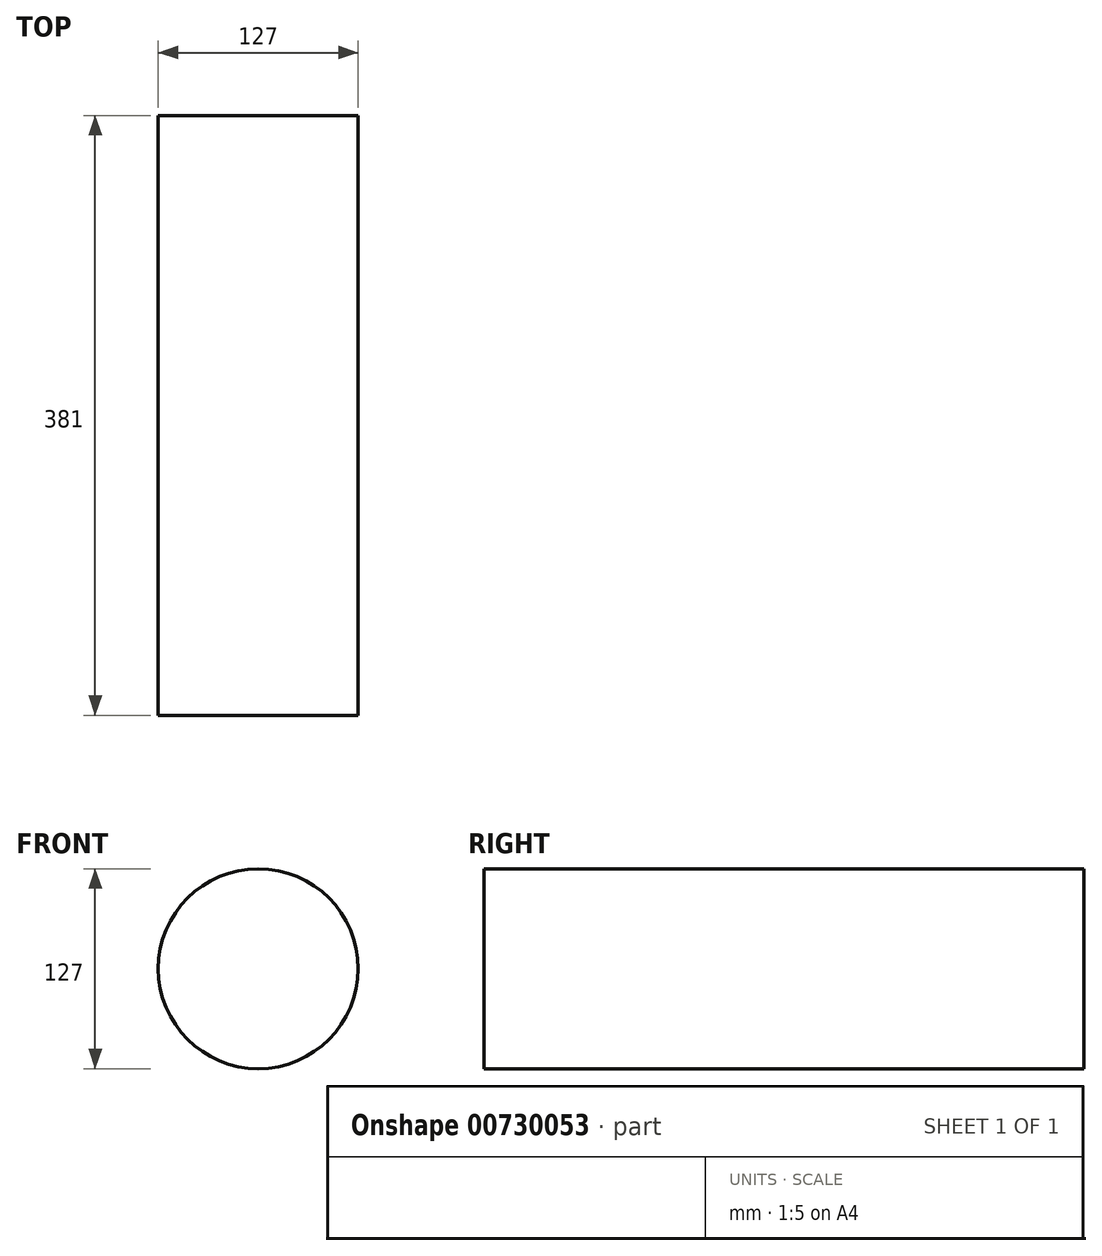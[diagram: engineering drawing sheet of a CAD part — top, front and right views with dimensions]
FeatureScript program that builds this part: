
annotation { "Feature Type Name" : "Feature", "Feature Type Description" : "" }
export const myFeature = defineFeature(function(context is Context, id is Id, definition is map)
    precondition{}
    {
        {
            var Q0;
            Q0=qCreatedBy(makeId("Front.planeOp"),FACE);
            var sketch = newSketch(context, id + "F0", { "sketchPlane" : qUnion([Q0])});
            skCircle(sketch, "E0", {"center": v(0, 0) * mm, "radius": 63.5 * mm});
            skSolve(sketch);
        }
        {
            var Q0;
            Q0 = qSketchRegion(id + "F0", true);
            extrude(context, id + "F1", {"entities" : qUnion([Q0]), "depth" : 381 * mm, "offsetDistance" : 25.4 * mm});
        }
    });
